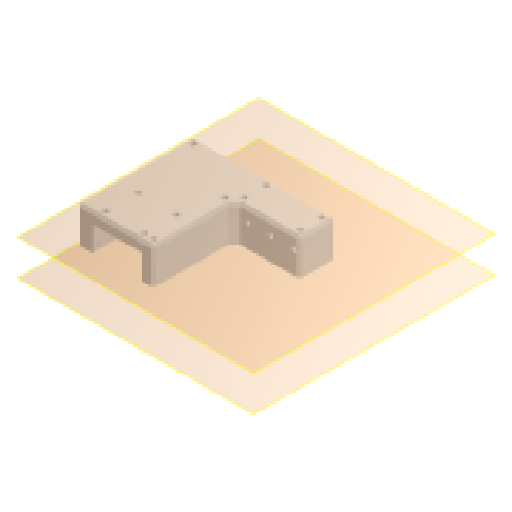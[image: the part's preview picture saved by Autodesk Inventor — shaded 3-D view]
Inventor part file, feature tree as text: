
AUTODESK INVENTOR PART (.ipt)
format: ipt  version: 2024.1 (Build 281209000, 209)  size: 335,360 bytes
history: native  units: mm
features: sketch x7, reference x7, other x6, projected_geometry x5, extrude x3, hole x3, plane x2, revolve x1, chamfer x1
ambient origin geometry x8: Origin, YZ Plane, XZ Plane, XY Plane, X Axis, Y Axis, Z Axis, Center Point
bodies: Volumenkörper1 (feature_tree)
feature tree (35):
  plane  "Arbeitsebene2"
  extrude  "Extrusion1"  TaperAngle=135.0deg  [1 undecoded]
  revolve  "Umdrehung1"
  chamfer  "Fasen1"  Distance=10.0mm
  hole  "Bohrung1"  [1 undecoded]
  extrude  "Extrusion2"  Depth=2.0mm TaperAngle=45.0deg
  hole  "Bohrung2"  [1 undecoded]
  hole  "Bohrung3"  [1 undecoded]
  extrude  "Extrusion3"  Depth=22.5mm
  plane  "Arbeitsebene1"
  sketch  "Skizze1"  dims[d0=25.0mm d1=135.0deg]
  reference  "Referenz1"
  reference  "Referenz2"
  reference  "Referenz3"
  reference  "Referenz4"
  sketch  "Skizze2"  dims[d2=8.0mm]
  reference  "Referenz5"
  sketch  "Skizze3"  dims[d3=0.0mm]
  projected_geometry  "Projizierte Kontur1"
  projected_geometry  "Projizierte Kontur2"
  projected_geometry  "Projizierte Kontur3"
  sketch  "Skizze4"  dims[d4=4.0mm]
  sketch  "Skizze5"  dims[d5=4.0mm]
  reference  "Referenz6"
  sketch  "Skizze6"  dims[d6=0.0mm d7=10.0mm d8=0.0mm]
  projected_geometry  "Projizierte Kontur4"
  sketch  "Skizze7"  dims[d9=35.0mm d10=360.0deg d11=2.0mm d12=2.0mm d13=45.0deg d14=3.0mm d15=3.2mm d16=6.0mm d17=4.0mm d18=6.0mm d19=90.0deg d20=1.0mm d21=0.0mm d24=35.0mm d25=0.0mm d26=22.5mm d27=3.2mm d28=6.0mm d29=6.5mm d30=16.0mm d31=90.0deg d32=8.0mm d33=0.0mm d34=0.3mm d35=2.0mm d36=2.8mm d37=6.0mm d38=6.5mm d39=16.0mm d40=90.0deg d41=20.0mm d42=0.0mm d43=20.0mm d44=35.0mm d45=0.0mm]
  reference  "Referenz7"
  projected_geometry  "Projizierte Kontur5"
  other  "Assembly_MicroscopeInABox_v0.iam"
  other  "00_Berrybase_CCTVLens_50mm:1"
  other  "Assembly_XYZ_Stage_Micrometer_ontop_lightsheet:1"
  other  "00_XYZstage_micro_LT-4047-S1:1"
  other  "00_10x_Objective_ViewSolutions_bm05073332:1"
  other  "40_XYZstage_micrometer_motorized_nema8_samplemount_lightsheet_screwed:1"
note: 4 required parameter values undecoded (feature->parameter linkage not recoverable at this tier; creation-order binding heuristic only, values carry confidence <= 0.55)
